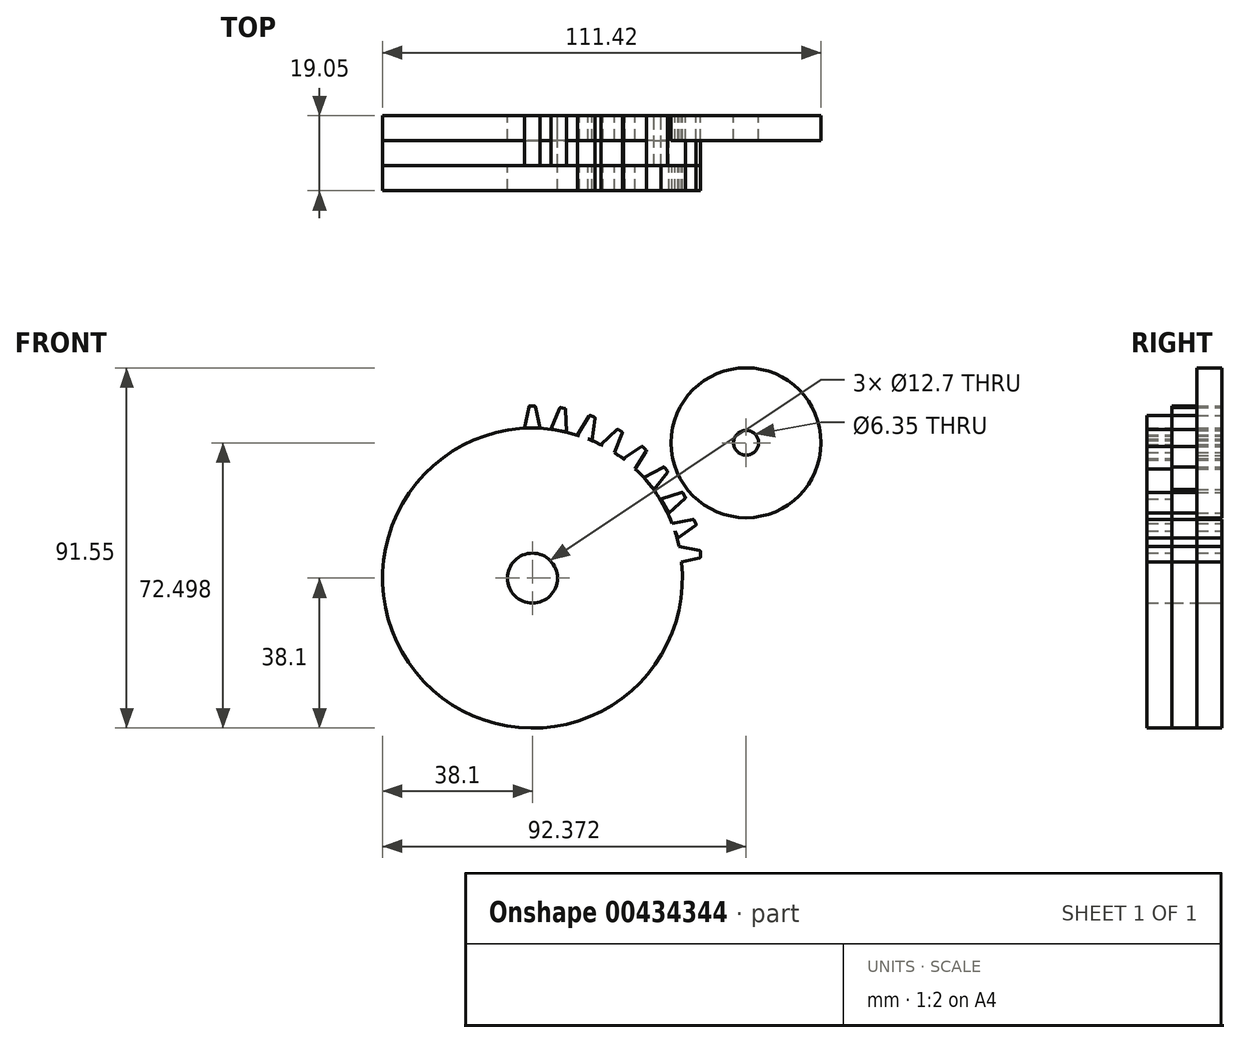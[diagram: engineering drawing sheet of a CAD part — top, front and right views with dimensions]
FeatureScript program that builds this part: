
annotation { "Feature Type Name" : "Feature", "Feature Type Description" : "" }
export const myFeature = defineFeature(function(context is Context, id is Id, definition is map)
    precondition{}
    {
        {
            var Q0;
            Q0=qCreatedBy(makeId("Front.planeOp"),FACE);
            var sketch = newSketch(context, id + "F0", { "sketchPlane" : qUnion([Q0])});
            skCircle(sketch, "E0", {"center": v(0, 0) * mm, "radius": 38.1 * mm});
            skCircle(sketch, "E1", {"center": v(0, 0) * mm, "radius": 6.35 * mm});
            skPoint(sketch, "E2", {"position": v(-116.36, 73.58) * mm});
            skLineSegment(sketch, "E3", {"start": v(-0.63, 43.78) * mm, "end": v(0.43, 43.78) * mm});
            skLineSegment(sketch, "E4", {"start": v(-0.93, 43.53) * mm, "end": v(-2.04, 38.15) * mm});
            skLineSegment(sketch, "E5", {"start": v(0.73, 43.54) * mm, "end": v(1.92, 38.15) * mm});
            skPoint(sketch, "E6.visualSharp", {"position": v(-0.88, 43.78) * mm});
            skArc(sketch, "E6.filletArc", {"start": v(-0.63, 43.78) * mm, "mid": v(-0.83, 43.7) * mm, "end": v(-0.93, 43.53) * mm});
            skPoint(sketch, "E7.visualSharp", {"position": v(0.68, 43.78) * mm});
            skArc(sketch, "E7.filletArc", {"start": v(0.73, 43.54) * mm, "mid": v(0.62, 43.7) * mm, "end": v(0.43, 43.78) * mm});
            skLineSegment(sketch, "E8", {"start": v(-2.04, 38.15) * mm, "end": v(1.92, 38.15) * mm});
            skLineSegment(sketch, "E9", {"start": v(7.15, 43.3) * mm, "end": v(8.2, 43.12) * mm});
            skLineSegment(sketch, "E10", {"start": v(6.81, 43.12) * mm, "end": v(4.73, 37.88) * mm});
            skLineSegment(sketch, "E11", {"start": v(8.45, 42.83) * mm, "end": v(8.69, 37.18) * mm});
            skPoint(sketch, "E12.visualSharp", {"position": v(6.9, 43.35) * mm});
            skArc(sketch, "E12.filletArc", {"start": v(7.15, 43.3) * mm, "mid": v(6.95, 43.27) * mm, "end": v(6.81, 43.12) * mm});
            skPoint(sketch, "E13.visualSharp", {"position": v(8.44, 43.08) * mm});
            skArc(sketch, "E13.filletArc", {"start": v(8.45, 42.83) * mm, "mid": v(8.37, 43.02) * mm, "end": v(8.2, 43.12) * mm});
            skLineSegment(sketch, "E14", {"start": v(4.73, 37.88) * mm, "end": v(8.69, 37.18) * mm});
            skLineSegment(sketch, "E15.0", {"start": v(4.73, 37.88) * mm, "end": v(8.69, 37.18) * mm, "construction": true});
            skLineSegment(sketch, "E16", {"start": v(14.7, 41.27) * mm, "end": v(15.7, 40.9) * mm});
            skLineSegment(sketch, "E17", {"start": v(14.33, 41.14) * mm, "end": v(11.4, 36.38) * mm});
            skLineSegment(sketch, "E18", {"start": v(15.9, 40.58) * mm, "end": v(15.15, 35.01) * mm});
            skPoint(sketch, "E19.visualSharp", {"position": v(14.46, 41.35) * mm});
            skArc(sketch, "E19.filletArc", {"start": v(14.7, 41.27) * mm, "mid": v(14.49, 41.27) * mm, "end": v(14.33, 41.14) * mm});
            skPoint(sketch, "E20.visualSharp", {"position": v(15.92, 40.82) * mm});
            skArc(sketch, "E20.filletArc", {"start": v(15.9, 40.58) * mm, "mid": v(15.85, 40.78) * mm, "end": v(15.7, 40.9) * mm});
            skLineSegment(sketch, "E21", {"start": v(11.4, 36.38) * mm, "end": v(15.15, 35.01) * mm});
            skLineSegment(sketch, "E22.0", {"start": v(11.4, 36.38) * mm, "end": v(15.15, 35.01) * mm, "construction": true});
            skLineSegment(sketch, "E23", {"start": v(21.81, 37.75) * mm, "end": v(22.7, 37.14) * mm});
            skLineSegment(sketch, "E24", {"start": v(21.43, 37.73) * mm, "end": v(17.43, 33.96) * mm});
            skLineSegment(sketch, "E25", {"start": v(22.8, 36.77) * mm, "end": v(20.68, 31.68) * mm});
            skPoint(sketch, "E26.visualSharp", {"position": v(21.6, 37.9) * mm});
            skArc(sketch, "E26.filletArc", {"start": v(21.81, 37.75) * mm, "mid": v(21.61, 37.8) * mm, "end": v(21.43, 37.73) * mm});
            skPoint(sketch, "E27.visualSharp", {"position": v(22.9, 37) * mm});
            skArc(sketch, "E27.filletArc", {"start": v(22.8, 36.77) * mm, "mid": v(22.81, 36.97) * mm, "end": v(22.7, 37.14) * mm});
            skLineSegment(sketch, "E28", {"start": v(17.43, 33.96) * mm, "end": v(20.68, 31.68) * mm});
            skLineSegment(sketch, "E29.0", {"start": v(17.43, 33.96) * mm, "end": v(20.68, 31.68) * mm, "construction": true});
            skLineSegment(sketch, "E30", {"start": v(28.08, 33.37) * mm, "end": v(28.86, 32.6) * mm});
            skLineSegment(sketch, "E31", {"start": v(27.7, 33.4) * mm, "end": v(23.1, 30.39) * mm});
            skLineSegment(sketch, "E32", {"start": v(28.9, 32.21) * mm, "end": v(25.93, 27.57) * mm});
            skPoint(sketch, "E33.visualSharp", {"position": v(27.9, 33.54) * mm});
            skArc(sketch, "E33.filletArc", {"start": v(28.08, 33.37) * mm, "mid": v(27.9, 33.46) * mm, "end": v(27.7, 33.4) * mm});
            skPoint(sketch, "E34.visualSharp", {"position": v(29.03, 32.42) * mm});
            skArc(sketch, "E34.filletArc", {"start": v(28.9, 32.21) * mm, "mid": v(28.95, 32.4) * mm, "end": v(28.86, 32.6) * mm});
            skLineSegment(sketch, "E35", {"start": v(23.1, 30.39) * mm, "end": v(25.93, 27.57) * mm});
            skLineSegment(sketch, "E36.0", {"start": v(23.1, 30.39) * mm, "end": v(25.93, 27.57) * mm, "construction": true});
            skLineSegment(sketch, "E37", {"start": v(33.53, 28.1) * mm, "end": v(34.25, 27.25) * mm});
            skLineSegment(sketch, "E38", {"start": v(33.16, 28.17) * mm, "end": v(28.32, 25.56) * mm});
            skLineSegment(sketch, "E39", {"start": v(34.26, 26.87) * mm, "end": v(30.9, 22.5) * mm});
            skPoint(sketch, "E40.visualSharp", {"position": v(33.37, 28.29) * mm});
            skArc(sketch, "E40.filletArc", {"start": v(33.53, 28.1) * mm, "mid": v(33.36, 28.2) * mm, "end": v(33.16, 28.17) * mm});
            skPoint(sketch, "E41.visualSharp", {"position": v(34.4, 27.06) * mm});
            skArc(sketch, "E41.filletArc", {"start": v(34.26, 26.87) * mm, "mid": v(34.32, 27.06) * mm, "end": v(34.25, 27.25) * mm});
            skLineSegment(sketch, "E42", {"start": v(28.32, 25.56) * mm, "end": v(30.9, 22.5) * mm});
            skLineSegment(sketch, "E43.0", {"start": v(28.32, 25.56) * mm, "end": v(30.9, 22.5) * mm, "construction": true});
            skLineSegment(sketch, "E44", {"start": v(38.24, 21.65) * mm, "end": v(38.8, 20.67) * mm});
            skLineSegment(sketch, "E45", {"start": v(37.88, 21.8) * mm, "end": v(32.66, 20.06) * mm});
            skLineSegment(sketch, "E46", {"start": v(38.75, 20.3) * mm, "end": v(34.68, 16.57) * mm});
            skPoint(sketch, "E47.visualSharp", {"position": v(38.11, 21.87) * mm});
            skArc(sketch, "E47.filletArc", {"start": v(38.24, 21.65) * mm, "mid": v(38.08, 21.79) * mm, "end": v(37.88, 21.8) * mm});
            skPoint(sketch, "E48.visualSharp", {"position": v(38.93, 20.46) * mm});
            skArc(sketch, "E48.filletArc", {"start": v(38.75, 20.3) * mm, "mid": v(38.84, 20.47) * mm, "end": v(38.8, 20.67) * mm});
            skLineSegment(sketch, "E49", {"start": v(32.66, 20.06) * mm, "end": v(34.68, 16.57) * mm});
            skLineSegment(sketch, "E50.0", {"start": v(32.66, 20.06) * mm, "end": v(34.68, 16.57) * mm, "construction": true});
            skLineSegment(sketch, "E51", {"start": v(41.1, 14.78) * mm, "end": v(41.55, 13.71) * mm});
            skLineSegment(sketch, "E52", {"start": v(40.75, 14.96) * mm, "end": v(35.37, 13.89) * mm});
            skLineSegment(sketch, "E53", {"start": v(41.44, 13.35) * mm, "end": v(36.95, 10.15) * mm});
            skPoint(sketch, "E54.visualSharp", {"position": v(41, 15.01) * mm});
            skArc(sketch, "E54.filletArc", {"start": v(41.1, 14.78) * mm, "mid": v(40.95, 14.93) * mm, "end": v(40.75, 14.96) * mm});
            skPoint(sketch, "E55.visualSharp", {"position": v(41.64, 13.49) * mm});
            skArc(sketch, "E55.filletArc", {"start": v(41.44, 13.35) * mm, "mid": v(41.56, 13.51) * mm, "end": v(41.55, 13.71) * mm});
            skLineSegment(sketch, "E56", {"start": v(35.37, 13.89) * mm, "end": v(36.95, 10.15) * mm});
            skLineSegment(sketch, "E57.0", {"start": v(35.37, 13.89) * mm, "end": v(36.95, 10.15) * mm, "construction": true});
            skLineSegment(sketch, "E58", {"start": v(42.73, 6.68) * mm, "end": v(42.73, 5.44) * mm});
            skLineSegment(sketch, "E59", {"start": v(42.48, 6.98) * mm, "end": v(37.22, 8.07) * mm});
            skLineSegment(sketch, "E60", {"start": v(42.49, 5.14) * mm, "end": v(37.22, 3.98) * mm});
            skPoint(sketch, "E61.visualSharp", {"position": v(42.73, 6.93) * mm});
            skArc(sketch, "E61.filletArc", {"start": v(42.73, 6.68) * mm, "mid": v(42.66, 6.88) * mm, "end": v(42.48, 6.98) * mm});
            skPoint(sketch, "E62.visualSharp", {"position": v(42.73, 5.2) * mm});
            skArc(sketch, "E62.filletArc", {"start": v(42.49, 5.14) * mm, "mid": v(42.66, 5.25) * mm, "end": v(42.73, 5.44) * mm});
            skLineSegment(sketch, "E63", {"start": v(37.22, 8.07) * mm, "end": v(37.22, 3.98) * mm});
            skLineSegment(sketch, "E64.0", {"start": v(37.22, 8.07) * mm, "end": v(37.22, 3.98) * mm, "construction": true});
            skSolve(sketch);
        }
        {
            var Q0;
            Q0 = qSketchRegion(id + "F0", true);
            extrude(context, id + "F1", {"entities" : qUnion([Q0]), "depth" : 12.7 * mm});
        }
        {
            var Q0;
            Q0=qCreatedBy(makeId("Front.planeOp"),FACE);
            var sketch = newSketch(context, id + "F2", { "sketchPlane" : qUnion([Q0])});
            skCircle(sketch, "E65", {"center": v(54.27, 34.4) * mm, "radius": 19.05 * mm});
            skCircle(sketch, "E66", {"center": v(54.27, 34.4) * mm, "radius": 3.18 * mm});
            skSolve(sketch);
        }
        {
            var Q0;
            Q0=makeQuery(id+"F2.imprint","IMPRINT",FACE,{"disambiguationData":[TD([[makeQuery(id+"F2.imprint","IMPRINT",EDGE,{"derivedFrom":sQuery(id+"F2.wireOp",EDGE,"E65")}),1.0]])]});
            var Q1;
            Q1=makeQuery(id+"F1.opExtrude","CAP_FACE",FACE,{"disambiguationData":[OSD([sQuery(id+"F0.wireOp",EDGE,"E0"),sQuery(id+"F0.wireOp",EDGE,"E1"),sQuery(id+"F0.wireOp",EDGE,"E16"),sQuery(id+"F0.wireOp",EDGE,"E17"),sQuery(id+"F0.wireOp",EDGE,"E18"),sQuery(id+"F0.wireOp",EDGE,"E19.filletArc"),sQuery(id+"F0.wireOp",EDGE,"E20.filletArc"),sQuery(id+"F0.wireOp",EDGE,"E21"),sQuery(id+"F0.wireOp",EDGE,"E23"),sQuery(id+"F0.wireOp",EDGE,"E24"),sQuery(id+"F0.wireOp",EDGE,"E25"),sQuery(id+"F0.wireOp",EDGE,"E26.filletArc"),sQuery(id+"F0.wireOp",EDGE,"E27.filletArc"),sQuery(id+"F0.wireOp",EDGE,"E28"),sQuery(id+"F0.wireOp",EDGE,"E30"),sQuery(id+"F0.wireOp",EDGE,"E31"),sQuery(id+"F0.wireOp",EDGE,"E32"),sQuery(id+"F0.wireOp",EDGE,"E33.filletArc"),sQuery(id+"F0.wireOp",EDGE,"E34.filletArc"),sQuery(id+"F0.wireOp",EDGE,"E35"),sQuery(id+"F0.wireOp",EDGE,"E51"),sQuery(id+"F0.wireOp",EDGE,"E52"),sQuery(id+"F0.wireOp",EDGE,"E53"),sQuery(id+"F0.wireOp",EDGE,"E54.filletArc"),sQuery(id+"F0.wireOp",EDGE,"E55.filletArc"),sQuery(id+"F0.wireOp",EDGE,"E56"),sQuery(id+"F0.wireOp",EDGE,"E58"),sQuery(id+"F0.wireOp",EDGE,"E59"),sQuery(id+"F0.wireOp",EDGE,"E60"),sQuery(id+"F0.wireOp",EDGE,"E61.filletArc"),sQuery(id+"F0.wireOp",EDGE,"E62.filletArc")])],"isStart":false});
            var Q2;
            Q2=makeQuery(id+"F1.opExtrude","CAP_FACE",FACE,{"disambiguationData":[OSD([sQuery(id+"F0.wireOp",EDGE,"E44"),sQuery(id+"F0.wireOp",EDGE,"E45"),sQuery(id+"F0.wireOp",EDGE,"E46"),sQuery(id+"F0.wireOp",EDGE,"E47.filletArc"),sQuery(id+"F0.wireOp",EDGE,"E48.filletArc"),sQuery(id+"F0.wireOp",EDGE,"E49")])],"isStart":false});
            var Q3;
            Q3=makeQuery(id+"F1.opExtrude","CAP_FACE",FACE,{"disambiguationData":[OSD([sQuery(id+"F0.wireOp",EDGE,"E0"),sQuery(id+"F0.wireOp",EDGE,"E1"),sQuery(id+"F0.wireOp",EDGE,"E16"),sQuery(id+"F0.wireOp",EDGE,"E17"),sQuery(id+"F0.wireOp",EDGE,"E18"),sQuery(id+"F0.wireOp",EDGE,"E19.filletArc"),sQuery(id+"F0.wireOp",EDGE,"E20.filletArc"),sQuery(id+"F0.wireOp",EDGE,"E21"),sQuery(id+"F0.wireOp",EDGE,"E23"),sQuery(id+"F0.wireOp",EDGE,"E24"),sQuery(id+"F0.wireOp",EDGE,"E25"),sQuery(id+"F0.wireOp",EDGE,"E26.filletArc"),sQuery(id+"F0.wireOp",EDGE,"E27.filletArc"),sQuery(id+"F0.wireOp",EDGE,"E28"),sQuery(id+"F0.wireOp",EDGE,"E30"),sQuery(id+"F0.wireOp",EDGE,"E31"),sQuery(id+"F0.wireOp",EDGE,"E32"),sQuery(id+"F0.wireOp",EDGE,"E33.filletArc"),sQuery(id+"F0.wireOp",EDGE,"E34.filletArc"),sQuery(id+"F0.wireOp",EDGE,"E35"),sQuery(id+"F0.wireOp",EDGE,"E51"),sQuery(id+"F0.wireOp",EDGE,"E52"),sQuery(id+"F0.wireOp",EDGE,"E53"),sQuery(id+"F0.wireOp",EDGE,"E54.filletArc"),sQuery(id+"F0.wireOp",EDGE,"E55.filletArc"),sQuery(id+"F0.wireOp",EDGE,"E56"),sQuery(id+"F0.wireOp",EDGE,"E58"),sQuery(id+"F0.wireOp",EDGE,"E59"),sQuery(id+"F0.wireOp",EDGE,"E60"),sQuery(id+"F0.wireOp",EDGE,"E61.filletArc"),sQuery(id+"F0.wireOp",EDGE,"E62.filletArc")])],"isStart":true});
            extrude(context, id + "F3", {"entities" : qUnion([Q0, Q1, Q2, Q3]), "depth" : 6.35 * mm});
        }
    });
